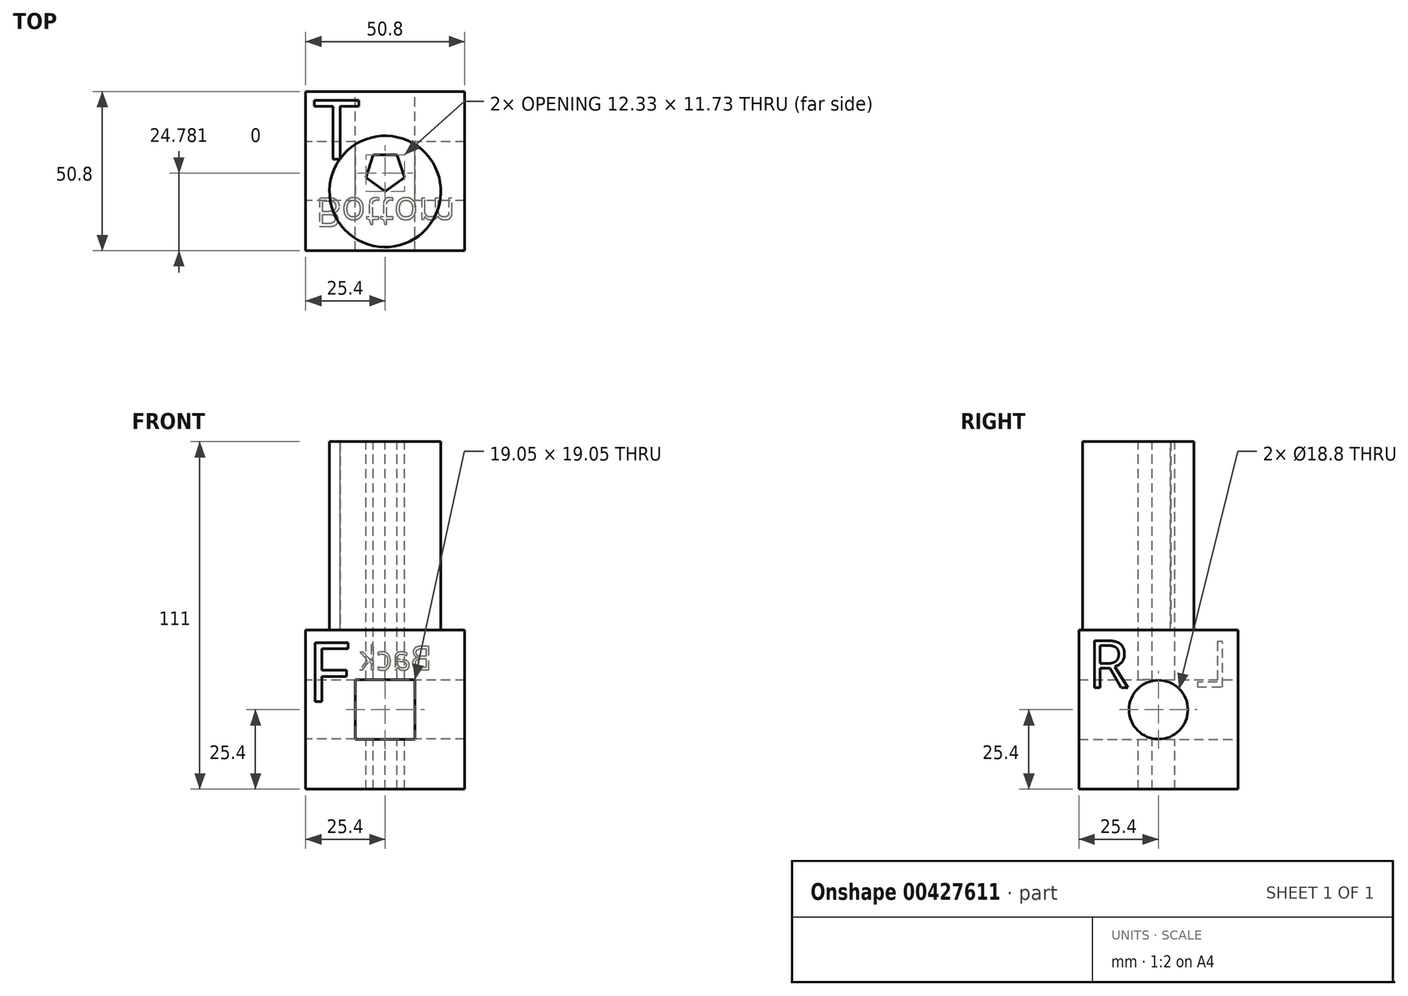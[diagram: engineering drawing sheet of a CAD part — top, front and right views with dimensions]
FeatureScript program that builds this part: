
annotation { "Feature Type Name" : "Feature", "Feature Type Description" : "" }
export const myFeature = defineFeature(function(context is Context, id is Id, definition is map)
    precondition{}
    {
        {
            var Q0;
            Q0=qCreatedBy(makeId("Front.planeOp"),FACE);
            var sketch = newSketch(context, id + "F0", { "sketchPlane" : qUnion([Q0])});
            skLineSegment(sketch, "E0.bottom", {"start": v(25.4, 25.4) * mm, "end": v(-25.4, 25.4) * mm});
            skLineSegment(sketch, "E0.top", {"start": v(25.4, -25.4) * mm, "end": v(-25.4, -25.4) * mm});
            skLineSegment(sketch, "E0.left", {"start": v(25.4, 25.4) * mm, "end": v(25.4, -25.4) * mm});
            skLineSegment(sketch, "E0.right", {"start": v(-25.4, 25.4) * mm, "end": v(-25.4, -25.4) * mm});
            skPoint(sketch, "E0.middle", {"position": v(0, 0) * mm});
            skLineSegment(sketch, "E1.bottom", {"start": v(9.52, 9.52) * mm, "end": v(-9.53, 9.52) * mm});
            skLineSegment(sketch, "E1.top", {"start": v(9.52, -9.52) * mm, "end": v(-9.53, -9.52) * mm});
            skLineSegment(sketch, "E1.left", {"start": v(9.52, 9.52) * mm, "end": v(9.52, -9.52) * mm});
            skLineSegment(sketch, "E1.right", {"start": v(-9.53, 9.52) * mm, "end": v(-9.53, -9.52) * mm});
            skSolve(sketch);
        }
        {
            var Q0;
            Q0=makeQuery(id+"F0.imprint","IMPRINT",FACE,{"disambiguationData":[TD([[makeQuery(id+"F0.imprint","IMPRINT",EDGE,{"derivedFrom":sQuery(id+"F0.wireOp",EDGE,"E0.bottom")}),1.0]])]});
            extrude(context, id + "F1", {"entities" : qUnion([Q0]), "depth" : 50.8 * mm, "symmetric" : true});
        }
        {
            var Q0;
            Q0=qCreatedBy(makeId("Right.planeOp"),FACE);
            var sketch = newSketch(context, id + "F2", { "sketchPlane" : qUnion([Q0])});
            skCircle(sketch, "E2", {"center": v(0, 0) * mm, "radius": 9.4 * mm});
            skSolve(sketch);
        }
        {
            var Q0;
            Q0=qSketchRegion(id+"F2",true);
            extrude(context, id + "F3", {"entities" : qUnion([Q0]), "operationType" : NewBodyOperationType.REMOVE, "depth" : 76.2 * mm, "symmetric" : true});
        }
        {
            var Q0;
            Q0=qCreatedBy(makeId("Top.planeOp"),FACE);
            var sketch = newSketch(context, id + "F4", { "sketchPlane" : qUnion([Q0])});
            skCircle(sketch, "E3.cCircle", {"center": v(0, 0) * mm, "radius": 5.24 * mm, "construction": true});
            skLineSegment(sketch, "E3.0", {"start": v(-3.8, 5.24) * mm, "end": v(3.8, 5.24) * mm});
            skLineSegment(sketch, "E3.1", {"start": v(3.8, 5.24) * mm, "end": v(6.16, -2) * mm});
            skLineSegment(sketch, "E3.2", {"start": v(6.16, -2) * mm, "end": v(0, -6.48) * mm});
            skLineSegment(sketch, "E3.3", {"start": v(0, -6.48) * mm, "end": v(-6.16, -2) * mm});
            skLineSegment(sketch, "E3.4", {"start": v(-6.16, -2) * mm, "end": v(-3.81, 5.24) * mm});
            skPoint(sketch, "E3.0.midPoint", {"position": v(0, 5.24) * mm});
            skSolve(sketch);
        }
        {
            var Q0;
            Q0=qSketchRegion(id+"F4",true);
            extrude(context, id + "F5", {"entities" : qUnion([Q0]), "operationType" : NewBodyOperationType.REMOVE, "oppositeDirection" : true, "depth" : 76.2 * mm, "symmetric" : true});
        }
        {
            var Q0;
            Q0=makeQuery(id+"F1.opExtrude","CAP_FACE",FACE,{"disambiguationData":[OSD([sQuery(id+"F0.wireOp",EDGE,"E0.bottom"),sQuery(id+"F0.wireOp",EDGE,"E0.top"),sQuery(id+"F0.wireOp",EDGE,"E0.left"),sQuery(id+"F0.wireOp",EDGE,"E0.right"),sQuery(id+"F0.wireOp",EDGE,"E1.bottom"),sQuery(id+"F0.wireOp",EDGE,"E1.top"),sQuery(id+"F0.wireOp",EDGE,"E1.left"),sQuery(id+"F0.wireOp",EDGE,"E1.right")])],"isStart":false});
            var sketch = newSketch(context, id + "F6", { "sketchPlane" : qUnion([Q0])});
            skText(sketch, "E4", { "text": "F", "fontName": "OpenSans-Regular.ttf"});
            const initialGuessF6  = {"E4": [-0.025, 0.00254, 1, 0, 0.01905]};
            skSetInitialGuess(sketch, initialGuessF6);
            skSolve(sketch);
        }
        {
            var Q0;
            Q0=qSketchRegion(id+"F6",true);
            extrude(context, id + "F7", {"entities" : qUnion([Q0]), "operationType" : NewBodyOperationType.REMOVE, "oppositeDirection" : true, "depth" : 0.03 * mm});
        }
        {
            var Q0;
            Q0=makeQuery(id+"F1.opExtrude","SWEPT_FACE",FACE,{"disambiguationData":[OSD([sQuery(id+"F0.wireOp",EDGE,"E0.bottom")])]});
            var sketch = newSketch(context, id + "F8", { "sketchPlane" : qUnion([Q0])});
            skText(sketch, "E5", { "text": "T", "fontName": "OpenSans-Regular.ttf"});
            const initialGuessF8  = {"E5": [-0.02283, 0.00378, 1, 0, 0.01905]};
            skSetInitialGuess(sketch, initialGuessF8);
            skSolve(sketch);
        }
        {
            var Q0;
            Q0=qSketchRegion(id+"F8",true);
            extrude(context, id + "F9", {"entities" : qUnion([Q0]), "operationType" : NewBodyOperationType.REMOVE, "oppositeDirection" : true, "depth" : 0.03 * mm});
        }
        {
            var Q0;
            Q0=makeQuery(id+"F1.opExtrude","CAP_FACE",FACE,{"disambiguationData":[OSD([sQuery(id+"F0.wireOp",EDGE,"E0.bottom"),sQuery(id+"F0.wireOp",EDGE,"E0.top"),sQuery(id+"F0.wireOp",EDGE,"E0.left"),sQuery(id+"F0.wireOp",EDGE,"E0.right"),sQuery(id+"F0.wireOp",EDGE,"E1.bottom"),sQuery(id+"F0.wireOp",EDGE,"E1.top"),sQuery(id+"F0.wireOp",EDGE,"E1.left"),sQuery(id+"F0.wireOp",EDGE,"E1.right")])],"isStart":true});
            var sketch = newSketch(context, id + "F10", { "sketchPlane" : qUnion([Q0])});
            skText(sketch, "E6", { "text": "Back", "fontName": "OpenSans-Regular.ttf"});
            const initialGuessF10  = {"E6": [-0.01502, 0.0127, 1, 0, 0.00762]};
            skSetInitialGuess(sketch, initialGuessF10);
            skSolve(sketch);
        }
        {
            var Q0;
            Q0=qSketchRegion(id+"F10",true);
            extrude(context, id + "F11", {"entities" : qUnion([Q0]), "operationType" : NewBodyOperationType.REMOVE, "oppositeDirection" : true, "depth" : 0.03 * mm});
        }
        {
            var Q0;
            Q0=makeQuery(id+"F1.opExtrude","SWEPT_FACE",FACE,{"disambiguationData":[OSD([sQuery(id+"F0.wireOp",EDGE,"E0.top")])]});
            var sketch = newSketch(context, id + "F12", { "sketchPlane" : qUnion([Q0])});
            skText(sketch, "E7", { "text": "Bottom", "fontName": "OpenSans-Regular.ttf"});
            const initialGuessF12  = {"E7": [-0.02223, 0.00857, 1, 0, 0.0092]};
            skSetInitialGuess(sketch, initialGuessF12);
            skSolve(sketch);
        }
        {
            var Q0;
            Q0=qSketchRegion(id+"F12",true);
            extrude(context, id + "F13", {"entities" : qUnion([Q0]), "operationType" : NewBodyOperationType.REMOVE, "oppositeDirection" : true, "depth" : 0.03 * mm});
        }
        {
            var Q0;
            Q0=makeQuery(id+"F1.opExtrude","SWEPT_FACE",FACE,{"disambiguationData":[OSD([sQuery(id+"F0.wireOp",EDGE,"E0.right")])]});
            var sketch = newSketch(context, id + "F14", { "sketchPlane" : qUnion([Q0])});
            skText(sketch, "E8", { "text": "L", "fontName": "OpenSans-Regular.ttf"});
            const initialGuessF14  = {"E8": [-0.0225, 0.0073, 1, 0, 0.0146]};
            skSetInitialGuess(sketch, initialGuessF14);
            skSolve(sketch);
        }
        {
            var Q0;
            Q0=qSketchRegion(id+"F14",true);
            extrude(context, id + "F15", {"entities" : qUnion([Q0]), "operationType" : NewBodyOperationType.REMOVE, "oppositeDirection" : true, "depth" : 0.03 * mm});
        }
        {
            var Q0;
            Q0=makeQuery(id+"F1.opExtrude","SWEPT_FACE",FACE,{"disambiguationData":[OSD([sQuery(id+"F0.wireOp",EDGE,"E0.left")])]});
            var sketch = newSketch(context, id + "F16", { "sketchPlane" : qUnion([Q0])});
            skText(sketch, "E9", { "text": "R", "fontName": "OpenSans-Regular.ttf"});
            const initialGuessF16  = {"E9": [-0.0225, 0.007, 1, 0, 0.0152]};
            skSetInitialGuess(sketch, initialGuessF16);
            skSolve(sketch);
        }
        {
            var Q0;
            Q0=qSketchRegion(id+"F16",true);
            extrude(context, id + "F17", {"entities" : qUnion([Q0]), "operationType" : NewBodyOperationType.REMOVE, "oppositeDirection" : true, "depth" : 0.03 * mm});
        }
        {
            var Q0;
            Q0=makeQuery(id+"F1.opExtrude","SWEPT_FACE",FACE,{"disambiguationData":[OSD([sQuery(id+"F0.wireOp",EDGE,"E0.bottom")])]});
            var sketch = newSketch(context, id + "F18", { "sketchPlane" : qUnion([Q0])});
            skCircle(sketch, "E10", {"center": v(0, -6.48) * mm, "radius": 17.78 * mm});
            skSolve(sketch);
        }
        {
            var Q0;
            {var subQ0=makeQuery(id+"F1.opExtrude","SWEPT_FACE",FACE,{"disambiguationData":[OSD([sQuery(id+"F0.wireOp",EDGE,"E0.bottom")])]});Q0=makeQuery(id+"F18.imprint","IMPRINT",FACE,{"disambiguationData":[TD([[makeQuery(id+"F18.imprint","IMPRINT",EDGE,{"derivedFrom":makeQuery(id+"F5.boolean.opBoolean","INTERSECT",EDGE,{"derivedFrom":[subQ0,makeQuery(id+"F5.opExtrude","SWEPT_FACE",FACE,{"disambiguationData":[OSD([sQuery(id+"F4.wireOp",EDGE,"E3.0")])]})]})}),-1.0]])]});}
            extrude(context, id + "F19", {"entities" : qUnion([Q0]), "operationType" : NewBodyOperationType.ADD, "depth" : 60.2 * mm});
        }
    });
